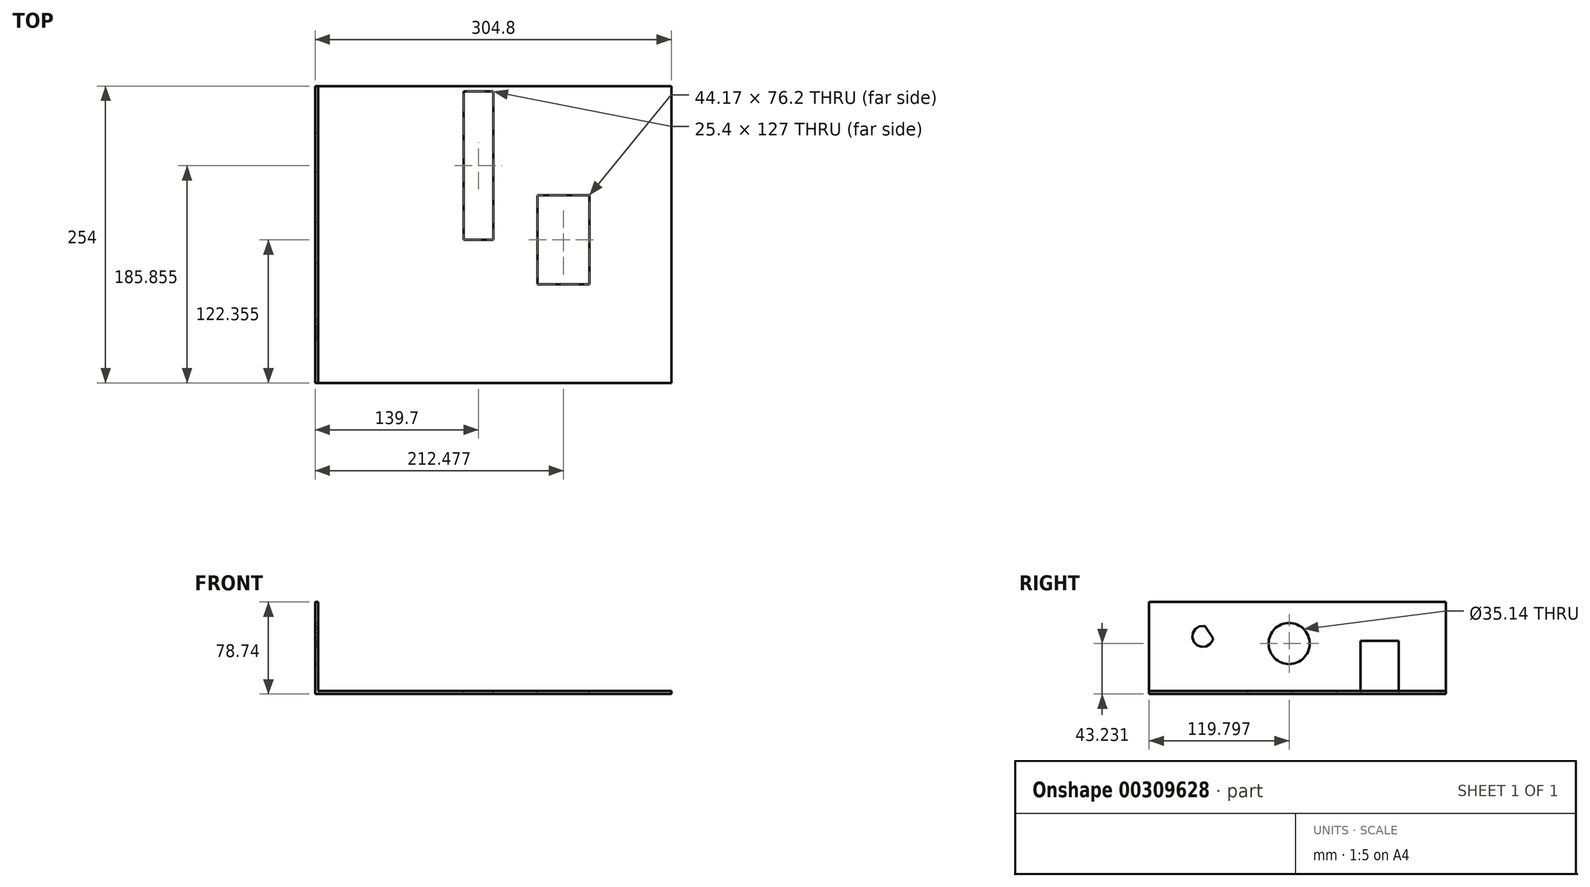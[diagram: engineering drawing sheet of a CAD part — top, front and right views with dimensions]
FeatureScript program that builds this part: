
annotation { "Feature Type Name" : "Feature", "Feature Type Description" : "" }
export const myFeature = defineFeature(function(context is Context, id is Id, definition is map)
    precondition{}
    {
        {
            var Q0;
            Q0=qCreatedBy(makeId("Top.planeOp"),FACE);
            var sketch = newSketch(context, id + "F0", { "sketchPlane" : qUnion([Q0])});
            skLineSegment(sketch, "E0.bottom", {"start": v(152.4, 127) * mm, "end": v(-152.4, 127) * mm});
            skLineSegment(sketch, "E0.top", {"start": v(152.4, -127) * mm, "end": v(-152.4, -127) * mm});
            skLineSegment(sketch, "E0.left", {"start": v(152.4, 127) * mm, "end": v(152.4, -127) * mm});
            skLineSegment(sketch, "E0.right", {"start": v(-152.4, 127) * mm, "end": v(-152.4, -127) * mm});
            skPoint(sketch, "E0.middle", {"position": v(0, 0) * mm});
            skSolve(sketch);
        }
        {
            var Q0;
            Q0=makeQuery(id+"F0.imprint","IMPRINT",FACE,{"disambiguationData":[TD([[makeQuery(id+"F0.imprint","IMPRINT",EDGE,{"derivedFrom":sQuery(id+"F0.wireOp",EDGE,"E0.bottom")}),1.0]])]});
            extrude(context, id + "F1", {"entities" : qUnion([Q0]), "depth" : 2.54 * mm});
        }
        {
            var Q0;
            Q0=makeQuery(id+"F1.opExtrude","CAP_FACE",FACE,{"disambiguationData":[OSD([sQuery(id+"F0.wireOp",EDGE,"E0.bottom"),sQuery(id+"F0.wireOp",EDGE,"E0.top"),sQuery(id+"F0.wireOp",EDGE,"E0.left"),sQuery(id+"F0.wireOp",EDGE,"E0.right")])],"isStart":false});
            var sketch = newSketch(context, id + "F2", { "sketchPlane" : qUnion([Q0])});
            skLineSegment(sketch, "E1.bottom", {"start": v(-152.4, 127) * mm, "end": v(-149.86, 127) * mm});
            skLineSegment(sketch, "E1.top", {"start": v(-152.4, -127) * mm, "end": v(-149.86, -127) * mm});
            skLineSegment(sketch, "E1.left", {"start": v(-152.4, 127) * mm, "end": v(-152.4, -127) * mm});
            skLineSegment(sketch, "E1.right", {"start": v(-149.86, 127) * mm, "end": v(-149.86, -127) * mm});
            skSolve(sketch);
        }
        {
            var Q0;
            Q0=makeQuery(id+"F2.imprint","IMPRINT",FACE,{"disambiguationData":[TD([[makeQuery(id+"F2.imprint","IMPRINT",EDGE,{"derivedFrom":sQuery(id+"F2.wireOp",EDGE,"E1.bottom")}),1.0]])]});
            extrude(context, id + "F3", {"entities" : qUnion([Q0]), "operationType" : NewBodyOperationType.ADD, "depth" : 76.2 * mm});
        }
        {
            var Q0;
            Q0=makeQuery(id+"F3.boolean.opBoolean","MERGE",FACE,{"derivedFrom":[makeQuery(id+"F1.opExtrude","SWEPT_FACE",FACE,{"disambiguationData":[OSD([sQuery(id+"F0.wireOp",EDGE,"E0.right")])]}),makeQuery(id+"F3.opExtrude","SWEPT_FACE",FACE,{"disambiguationData":[OSD([sQuery(id+"F2.wireOp",EDGE,"E1.left")])]})]});
            var sketch = newSketch(context, id + "F4", { "sketchPlane" : qUnion([Q0])});
            skLineSegment(sketch, "E2.bottom", {"start": v(-86.7, 45.47) * mm, "end": v(-53.74, 45.47) * mm});
            skLineSegment(sketch, "E2.top", {"start": v(-86.7, 0) * mm, "end": v(-53.74, 0) * mm});
            skLineSegment(sketch, "E2.left", {"start": v(-86.7, 45.47) * mm, "end": v(-86.7, 0) * mm});
            skLineSegment(sketch, "E2.right", {"start": v(-53.74, 45.47) * mm, "end": v(-53.74, 0) * mm});
            skSolve(sketch);
        }
        {
            var Q0;
            Q0=makeQuery(id+"F4.imprint","IMPRINT",FACE,{"disambiguationData":[TD([[makeQuery(id+"F4.imprint","IMPRINT",EDGE,{"derivedFrom":sQuery(id+"F4.wireOp",EDGE,"E2.bottom")}),-1.0]])]});
            extrude(context, id + "F5", {"entities" : qUnion([Q0]), "operationType" : NewBodyOperationType.REMOVE, "oppositeDirection" : true, "depth" : 2.54 * mm});
        }
        {
            var Q0;
            Q0=makeQuery(id+"F3.boolean.opBoolean","MERGE",FACE,{"derivedFrom":[makeQuery(id+"F1.opExtrude","SWEPT_FACE",FACE,{"disambiguationData":[OSD([sQuery(id+"F0.wireOp",EDGE,"E0.right")])]}),makeQuery(id+"F3.opExtrude","SWEPT_FACE",FACE,{"disambiguationData":[OSD([sQuery(id+"F2.wireOp",EDGE,"E1.left")])]})]});
            var sketch = newSketch(context, id + "F6", { "sketchPlane" : qUnion([Q0])});
            skCircle(sketch, "E3", {"center": v(7.2, 43.23) * mm, "radius": 17.57 * mm});
            skSolve(sketch);
        }
        {
            var Q0;
            Q0=makeQuery(id+"F6.imprint","IMPRINT",FACE,{"disambiguationData":[TD([[makeQuery(id+"F6.imprint","IMPRINT",EDGE,{"derivedFrom":sQuery(id+"F6.wireOp",EDGE,"E3")}),1.0]])]});
            extrude(context, id + "F7", {"entities" : qUnion([Q0]), "operationType" : NewBodyOperationType.REMOVE, "oppositeDirection" : true, "depth" : 25.4 * mm});
        }
        {
            var Q0;
            Q0=makeQuery(id+"F3.opExtrude","SWEPT_FACE",FACE,{"disambiguationData":[OSD([sQuery(id+"F2.wireOp",EDGE,"E1.right")])]});
            var sketch = newSketch(context, id + "F8", { "sketchPlane" : qUnion([Q0])});
            skCircle(sketch, "E4.cCircle", {"center": v(-81.07, 49.26) * mm, "radius": 8.8 * mm, "construction": true});
            skLineSegment(sketch, "E4.0", {"start": v(-72.55, 46.3) * mm, "end": v(-74.68, 42.9) * mm});
            skLineSegment(sketch, "E4.1", {"start": v(-74.68, 42.9) * mm, "end": v(-78.07, 40.76) * mm});
            skLineSegment(sketch, "E4.2", {"start": v(-78.07, 40.76) * mm, "end": v(-82.06, 40.3) * mm});
            skLineSegment(sketch, "E4.3", {"start": v(-82.06, 40.3) * mm, "end": v(-85.85, 41.61) * mm});
            skLineSegment(sketch, "E4.4", {"start": v(-85.85, 41.61) * mm, "end": v(-88.7, 44.44) * mm});
            skLineSegment(sketch, "E4.5", {"start": v(-88.7, 44.44) * mm, "end": v(-90.03, 48.23) * mm});
            skLineSegment(sketch, "E4.6", {"start": v(-90.03, 48.23) * mm, "end": v(-89.59, 52.22) * mm});
            skLineSegment(sketch, "E4.7", {"start": v(-89.59, 52.22) * mm, "end": v(-87.46, 55.62) * mm});
            skLineSegment(sketch, "E4.8", {"start": v(-87.46, 55.62) * mm, "end": v(-84.07, 57.76) * mm});
            skLineSegment(sketch, "E4.9", {"start": v(-84.07, 57.76) * mm, "end": v(-80.08, 58.22) * mm});
            skLineSegment(sketch, "E4.10", {"start": v(-80.08, 58.22) * mm, "end": v(-76.3, 56.9) * mm});
            skLineSegment(sketch, "E4.11", {"start": v(-76.3, 56.9) * mm, "end": v(-73.45, 54.08) * mm});
            skLineSegment(sketch, "E4.12", {"start": v(-73.45, 54.08) * mm, "end": v(-72.11, 50.3) * mm});
            skLineSegment(sketch, "E4.13", {"start": v(-72.11, 50.3) * mm, "end": v(-72.55, 46.3) * mm});
            skPoint(sketch, "E4.0.midPoint", {"position": v(-73.62, 44.6) * mm});
            skCircle(sketch, "E5.cCircle", {"center": v(-56.84, 53.45) * mm, "radius": 15.77 * mm, "construction": true});
            skLineSegment(sketch, "E5.0", {"start": v(-34.94, 49.26) * mm, "end": v(-61.04, 31.55) * mm});
            skLineSegment(sketch, "E5.1", {"start": v(-61.04, 31.55) * mm, "end": v(-78.74, 57.65) * mm});
            skLineSegment(sketch, "E5.2", {"start": v(-78.74, 57.65) * mm, "end": v(-52.65, 75.35) * mm});
            skLineSegment(sketch, "E5.3", {"start": v(-52.65, 75.35) * mm, "end": v(-34.94, 49.26) * mm});
            skPoint(sketch, "E5.0.midPoint", {"position": v(-47.99, 40.4) * mm});
            skSolve(sketch);
        }
        {
            var Q0;
            Q0=makeQuery(id+"F8.imprint","IMPRINT",FACE,{"disambiguationData":[TD([[makeQuery(id+"F8.imprint","IMPRINT",EDGE,{"derivedFrom":sQuery(id+"F8.wireOp",EDGE,"E4.0")}),-1.0]])]});
            extrude(context, id + "F9", {"entities" : qUnion([Q0]), "operationType" : NewBodyOperationType.REMOVE, "oppositeDirection" : true, "depth" : 25.4 * mm});
        }
        {
            var Q0;
            {var subQ0=sQuery(id+"F2.wireOp",EDGE,"E1.right");Q0=makeQuery(id+"F2.imprint","IMPRINT",FACE,{"disambiguationData":[TD([[makeQuery(id+"F2.imprint","IMPRINT",EDGE,{"derivedFrom":subQ0}),1.0]])]});}
            var sketch = newSketch(context, id + "F10", { "sketchPlane" : qUnion([Q0])});
            skLineSegment(sketch, "E6.bottom", {"start": v(0, -4.64) * mm, "end": v(-25.4, -4.64) * mm});
            skLineSegment(sketch, "E6.top", {"start": v(0, 122.36) * mm, "end": v(-25.4, 122.36) * mm});
            skLineSegment(sketch, "E6.left", {"start": v(0, -4.64) * mm, "end": v(0, 122.36) * mm});
            skLineSegment(sketch, "E6.right", {"start": v(-25.4, -4.64) * mm, "end": v(-25.4, 122.36) * mm});
            skPoint(sketch, "E6.middle", {"position": v(-12.7, 58.86) * mm});
            skLineSegment(sketch, "E7.bottom", {"start": v(82.16, 33.46) * mm, "end": v(38, 33.46) * mm});
            skLineSegment(sketch, "E7.top", {"start": v(82.16, -42.74) * mm, "end": v(38, -42.74) * mm});
            skLineSegment(sketch, "E7.left", {"start": v(82.16, 33.46) * mm, "end": v(82.16, -42.74) * mm});
            skLineSegment(sketch, "E7.right", {"start": v(38, 33.46) * mm, "end": v(38, -42.74) * mm});
            skPoint(sketch, "E7.middle", {"position": v(60.08, -4.64) * mm});
            skSolve(sketch);
        }
        {
            var Q0;
            Q0 = qSketchRegion(id + "F10", true);
            extrude(context, id + "F11", {"entities" : qUnion([Q0]), "operationType" : NewBodyOperationType.REMOVE, "oppositeDirection" : true, "depth" : 25.4 * mm});
        }
    });
